SOLIDWORKS PART (.sldprt)
format: sldprt  version: not decoded by parser v0  size: 228,864 bytes
history: native  units: mm
features: extrude x6, sketch x5, plane x3, fillet x3, mirror x2, material x1 (+8 scaffold rows collapsed)
feature tree (28):
  scaffold x8  (default folders/planes/origin — collapsed)
  material  "Duranickel(R) 301"
  plane  "Alzado"
  plane  "Planta"
  plane  "Vista lateral"
  sketch  "Croquis1"  dims[D5=3.5mm D6=1.0mm D7=1.0mm D8=1.0mm D9=1.0mm D1=7.0mm D2=6.5mm D3=3.5mm D4=3.25mm D10=5.0mm D11=5.0mm D12=2.5mm D13=2.5mm D14=5.0mm]
  extrude  "Extruir1"  Depth=0.2mm
  sketch  "Croquis2"  dims[c1.D1=3.1mm c1.D2=5.5mm c2.D1=7.1mm]
  extrude  "Extruir2"  Depth=0.2mm
  mirror  "Simetría1"
  fillet  "Redondeo1"  Radius=0.2mm
  sketch  "Croquis3"
  extrude  "Extruir3"  Depth=3mm
  sketch  "Croquis4"
  extrude  "Extruir5"  Depth=1mm
  sketch  "Croquis5"  dims[D1=1.0mm D2=1.0mm D3=1.0mm D4=1.0mm]
  extrude  "Extruir6"  Depth=0.4mm
  extrude  "Redondeo2"  Depth=0.2mm
  fillet  "PW2_UID_val"  [1 undecoded]
  mirror  "pw2 (2)"
  fillet  "PW2_UID_val"  [1 undecoded]
decode coverage: 10 of 16 modeling features carry decoded parameters
note: 2 parameter values undecoded
note: suppression state not decoded; provenance and decode notes live in map.json
